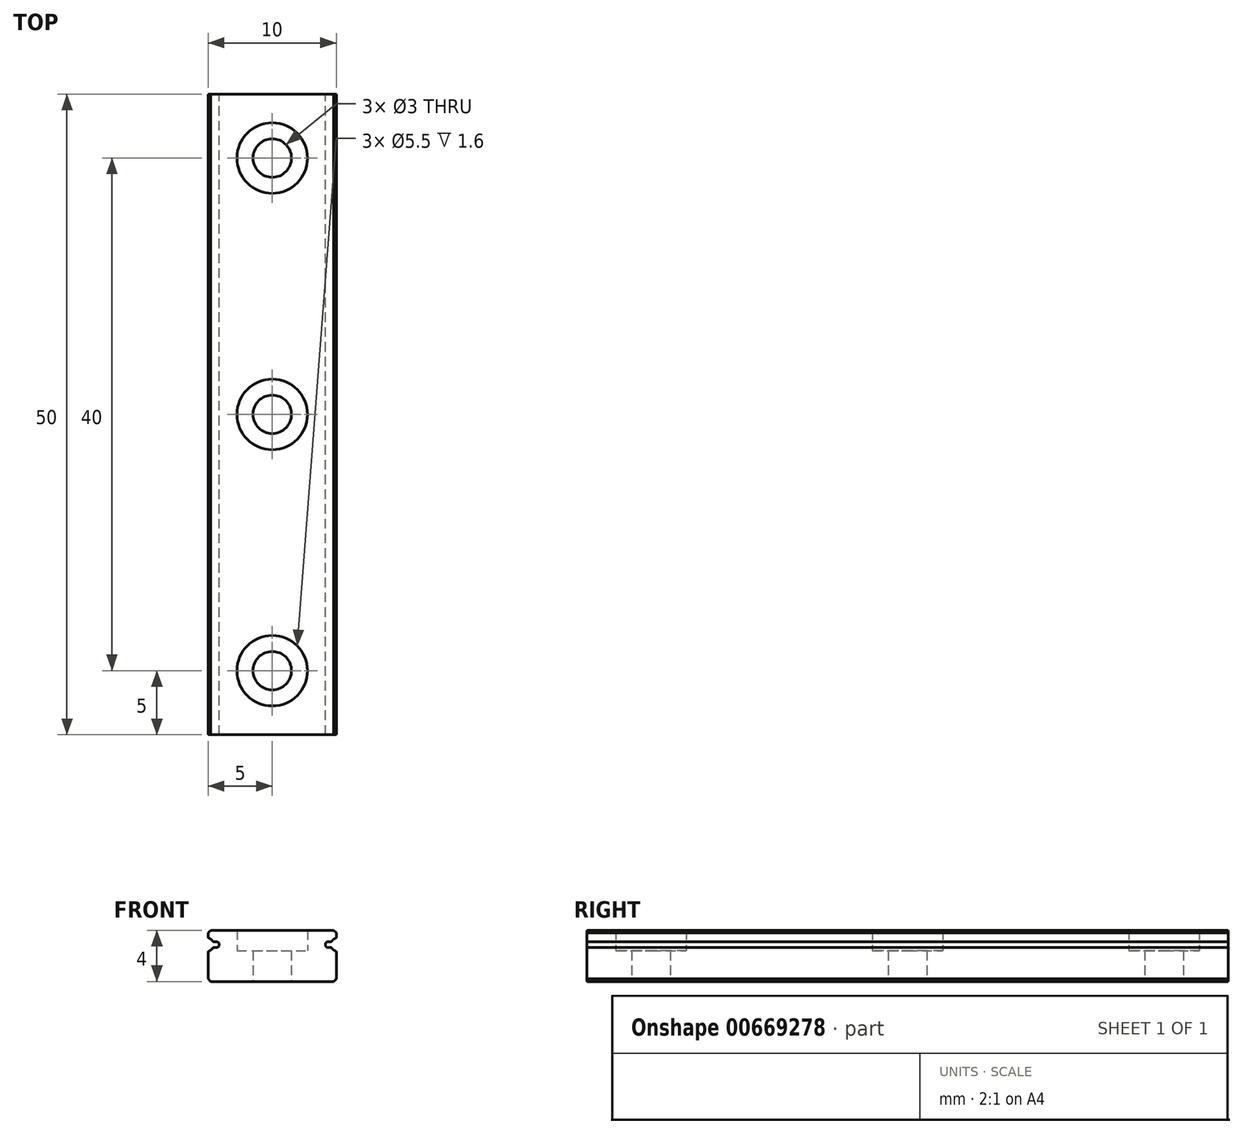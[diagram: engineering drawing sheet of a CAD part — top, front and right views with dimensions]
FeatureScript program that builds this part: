
annotation { "Feature Type Name" : "Feature", "Feature Type Description" : "" }
export const myFeature = defineFeature(function(context is Context, id is Id, definition is map)
    precondition{}
    {
        {
            var Q0;
            Q0=qCreatedBy(makeId("Front.planeOp"),FACE);
            var sketch = newSketch(context, id + "F0", { "sketchPlane" : qUnion([Q0])});
            skLineSegment(sketch, "E0.bottom", {"start": v(0, -2) * mm, "end": v(-4.79, -2) * mm});
            skLineSegment(sketch, "E0.right", {"start": v(-5, -1.79) * mm, "end": v(-5, 0.28) * mm});
            skPoint(sketch, "E0.middle", {"position": v(0, 0) * mm});
            skArc(sketch, "E1", {"start": v(-4.93, 0.38) * mm, "mid": v(-4.78, 0.46) * mm, "end": v(-4.66, 0.6) * mm});
            skArc(sketch, "E2", {"start": v(-4.37, 0.64) * mm, "mid": v(-4.14, 0.88) * mm, "end": v(-4.37, 1.11) * mm});
            skLineSegment(sketch, "E3", {"start": v(-4.37, 0.64) * mm, "end": v(-4.57, 0.64) * mm});
            skLineSegment(sketch, "E4", {"start": v(-4.37, 1.11) * mm, "end": v(-4.57, 1.11) * mm});
            skLineSegment(sketch, "E5", {"start": v(-5, 1.79) * mm, "end": v(-4.79, 2) * mm});
            skLineSegment(sketch, "E6.MirrorCS", {"start": v(-5, -1.79) * mm, "end": v(-4.79, -2) * mm});
            skPoint(sketch, "E7.orphan", {"position": v(-5, 2) * mm});
            skLineSegment(sketch, "E8.trimOffspring", {"start": v(-5, 1.47) * mm, "end": v(-5, 1.79) * mm});
            skArc(sketch, "E9.trimOffspring", {"start": v(-4.66, 1.16) * mm, "mid": v(-4.78, 1.29) * mm, "end": v(-4.93, 1.37) * mm});
            skPoint(sketch, "E10.orphan", {"position": v(-5, -2) * mm});
            skLineSegment(sketch, "E11", {"start": v(-4.79, 2) * mm, "end": v(0, 2) * mm});
            skLineSegment(sketch, "E12.MirrorCS", {"start": v(4.37, 0.64) * mm, "end": v(4.57, 0.64) * mm});
            skLineSegment(sketch, "E13.MirrorCS", {"start": v(5, -1.79) * mm, "end": v(4.79, -2) * mm});
            skLineSegment(sketch, "E14.MirrorCS", {"start": v(4.37, 1.11) * mm, "end": v(4.57, 1.11) * mm});
            skLineSegment(sketch, "E15.MirrorCS", {"start": v(5, 1.79) * mm, "end": v(4.79, 2) * mm});
            skArc(sketch, "E16.MirrorCS", {"start": v(4.93, 0.38) * mm, "mid": v(4.78, 0.46) * mm, "end": v(4.66, 0.6) * mm});
            skLineSegment(sketch, "E17.MirrorCS", {"start": v(4.79, 2) * mm, "end": v(0, 2) * mm});
            skPoint(sketch, "E18.MirrorP", {"position": v(5, -2) * mm});
            skArc(sketch, "E19.MirrorCS", {"start": v(4.66, 1.16) * mm, "mid": v(4.78, 1.29) * mm, "end": v(4.93, 1.37) * mm});
            skArc(sketch, "E20.MirrorCS", {"start": v(4.37, 0.64) * mm, "mid": v(4.14, 0.88) * mm, "end": v(4.37, 1.11) * mm});
            skPoint(sketch, "E21.MirrorP", {"position": v(5, 2) * mm});
            skLineSegment(sketch, "E22.MirrorCS", {"start": v(0, -2) * mm, "end": v(4.79, -2) * mm});
            skLineSegment(sketch, "E23.MirrorCS", {"start": v(5, -1.79) * mm, "end": v(5, 0.28) * mm});
            skLineSegment(sketch, "E24.MirrorCS", {"start": v(5, 1.47) * mm, "end": v(5, 1.79) * mm});
            skPoint(sketch, "E25.0.visualSharp", {"position": v(-5, 1.4) * mm});
            skArc(sketch, "E25.0.filletArc", {"start": v(-5, 1.47) * mm, "mid": v(-4.98, 1.4) * mm, "end": v(-4.93, 1.37) * mm});
            skPoint(sketch, "E25.1.visualSharp", {"position": v(-4.63, 1.11) * mm});
            skArc(sketch, "E25.1.filletArc", {"start": v(-4.66, 1.16) * mm, "mid": v(-4.62, 1.12) * mm, "end": v(-4.57, 1.11) * mm});
            skPoint(sketch, "E25.2.visualSharp", {"position": v(-4.63, 0.64) * mm});
            skArc(sketch, "E25.2.filletArc", {"start": v(-4.57, 0.64) * mm, "mid": v(-4.62, 0.63) * mm, "end": v(-4.66, 0.6) * mm});
            skPoint(sketch, "E25.3.visualSharp", {"position": v(-5, 0.36) * mm});
            skArc(sketch, "E25.3.filletArc", {"start": v(-4.93, 0.38) * mm, "mid": v(-4.98, 0.34) * mm, "end": v(-5, 0.28) * mm});
            skPoint(sketch, "E25.4.visualSharp", {"position": v(5, 1.4) * mm});
            skArc(sketch, "E25.4.filletArc", {"start": v(4.93, 1.37) * mm, "mid": v(4.98, 1.4) * mm, "end": v(5, 1.47) * mm});
            skPoint(sketch, "E25.5.visualSharp", {"position": v(4.63, 1.11) * mm});
            skArc(sketch, "E25.5.filletArc", {"start": v(4.57, 1.11) * mm, "mid": v(4.62, 1.12) * mm, "end": v(4.66, 1.16) * mm});
            skPoint(sketch, "E25.6.visualSharp", {"position": v(4.63, 0.64) * mm});
            skArc(sketch, "E25.6.filletArc", {"start": v(4.66, 0.6) * mm, "mid": v(4.62, 0.63) * mm, "end": v(4.57, 0.64) * mm});
            skPoint(sketch, "E25.7.visualSharp", {"position": v(5, 0.36) * mm});
            skArc(sketch, "E25.7.filletArc", {"start": v(5, 0.28) * mm, "mid": v(4.98, 0.34) * mm, "end": v(4.93, 0.38) * mm});
            skSolve(sketch);
        }
        {
            var Q0;
            Q0=makeQuery(id+"F0.imprint","IMPRINT",FACE,{"disambiguationData":[TD([[makeQuery(id+"F0.imprint","IMPRINT",EDGE,{"derivedFrom":sQuery(id+"F0.wireOp",EDGE,"E0.bottom")}),-1.0]])]});
            extrude(context, id + "F1", {"entities" : qUnion([Q0]), "depth" : 50 * mm, "offsetDistance" : 25 * mm});
        }
        {
            var Q0;
            Q0=makeQuery(id+"F1.opExtrude","SWEPT_FACE",FACE,{"disambiguationData":[OSD([sQuery(id+"F0.wireOp",EDGE,"E11"),sQuery(id+"F0.wireOp",EDGE,"E17.MirrorCS")])]});
            var sketch = newSketch(context, id + "F2", { "sketchPlane" : qUnion([Q0])});
            skPoint(sketch, "E26", {"position": v(0, -5) * mm});
            skPoint(sketch, "E27.1.0.0", {"position": v(0, -25) * mm});
            skPoint(sketch, "E27.2.0.0", {"position": v(0, -45) * mm});
            skLineSegment(sketch, "E27.direction1", {"start": v(0, -5) * mm, "end": v(0, -25) * mm, "construction": true});
            skPoint(sketch, "E28.0.3.0", {"position": v(0, -65) * mm});
            skPoint(sketch, "E28.0.4.0", {"position": v(0, -85) * mm});
            skPoint(sketch, "E28.0.5.0", {"position": v(0, -105) * mm});
            skPoint(sketch, "E28.0.6.0", {"position": v(0, -125) * mm});
            skPoint(sketch, "E28.0.7.0", {"position": v(0, -145) * mm});
            skPoint(sketch, "E28.0.8.0", {"position": v(0, -165) * mm});
            skPoint(sketch, "E28.0.9.0", {"position": v(0, -185) * mm});
            skPoint(sketch, "E28.0.10.0", {"position": v(0, -205) * mm});
            skPoint(sketch, "E28.0.11.0", {"position": v(0, -225) * mm});
            skPoint(sketch, "E28.0.12.0", {"position": v(0, -245) * mm});
            skSolve(sketch);
        }
        {
            var Q0;
            Q0=sQuery(id+"F2.wireOp",VERTEX,"E28.0.5.0");
            var Q1;
            Q1=sQuery(id+"F2.wireOp",VERTEX,"E28.0.6.0");
            var Q2;
            Q2=sQuery(id+"F2.wireOp",VERTEX,"E28.0.7.0");
            var Q3;
            Q3=sQuery(id+"F2.wireOp",VERTEX,"E28.0.8.0");
            var Q4;
            Q4=sQuery(id+"F2.wireOp",VERTEX,"E28.0.9.0");
            var Q5;
            Q5=sQuery(id+"F2.wireOp",VERTEX,"E28.0.10.0");
            var Q6;
            Q6=sQuery(id+"F2.wireOp",VERTEX,"E28.0.11.0");
            var Q7;
            Q7=sQuery(id+"F2.wireOp",VERTEX,"E28.0.12.0");
            var Q8;
            Q8=sQuery(id+"F2.wireOp",VERTEX,"E26");
            var Q9;
            Q9=sQuery(id+"F2.wireOp",VERTEX,"E27.1.0.0");
            var Q10;
            Q10=sQuery(id+"F2.wireOp",VERTEX,"E27.2.0.0");
            var Q11;
            Q11=sQuery(id+"F2.wireOp",VERTEX,"E28.0.3.0");
            var Q12;
            Q12=sQuery(id+"F2.wireOp",VERTEX,"E28.0.4.0");
            var Q13;
            Q13=makeQuery(id+"F1.opExtrude","SWEPT_BODY",BODY,{"disambiguationData":[OSD([sQuery(id+"F0.wireOp",EDGE,"E0.bottom"),sQuery(id+"F0.wireOp",EDGE,"E0.right"),sQuery(id+"F0.wireOp",EDGE,"E1"),sQuery(id+"F0.wireOp",EDGE,"E2"),sQuery(id+"F0.wireOp",EDGE,"E3"),sQuery(id+"F0.wireOp",EDGE,"E4"),sQuery(id+"F0.wireOp",EDGE,"E5"),sQuery(id+"F0.wireOp",EDGE,"E6.MirrorCS"),sQuery(id+"F0.wireOp",EDGE,"E8.trimOffspring"),sQuery(id+"F0.wireOp",EDGE,"E9.trimOffspring"),sQuery(id+"F0.wireOp",EDGE,"E11"),sQuery(id+"F0.wireOp",EDGE,"E12.MirrorCS"),sQuery(id+"F0.wireOp",EDGE,"E13.MirrorCS"),sQuery(id+"F0.wireOp",EDGE,"E14.MirrorCS"),sQuery(id+"F0.wireOp",EDGE,"E15.MirrorCS"),sQuery(id+"F0.wireOp",EDGE,"E16.MirrorCS"),sQuery(id+"F0.wireOp",EDGE,"E17.MirrorCS"),sQuery(id+"F0.wireOp",EDGE,"E19.MirrorCS"),sQuery(id+"F0.wireOp",EDGE,"E20.MirrorCS"),sQuery(id+"F0.wireOp",EDGE,"E22.MirrorCS"),sQuery(id+"F0.wireOp",EDGE,"E23.MirrorCS"),sQuery(id+"F0.wireOp",EDGE,"E24.MirrorCS")])]});
            hole(context, id + "F3", {"style" : HoleStyle.C_BORE, "endStyle" : HoleEndStyle.THROUGH, "holeDiameter" : 3 * mm, "cBoreDiameter" : 5.5 * mm, "cBoreDepth" : 1.6 * mm, "majorDiameter" : 2.5 * mm, "isTappedThrough" : true, "tappedDepth" : 1 * mm, "tapClearance" : 3, "locations" : qUnion([Q0, Q1, Q2, Q3, Q4, Q5, Q6, Q7, Q8, Q9, Q10, Q11, Q12]), "scope" : qUnion([Q13]), "startStyle" : HoleStartStyle.PART});
        }
    });
